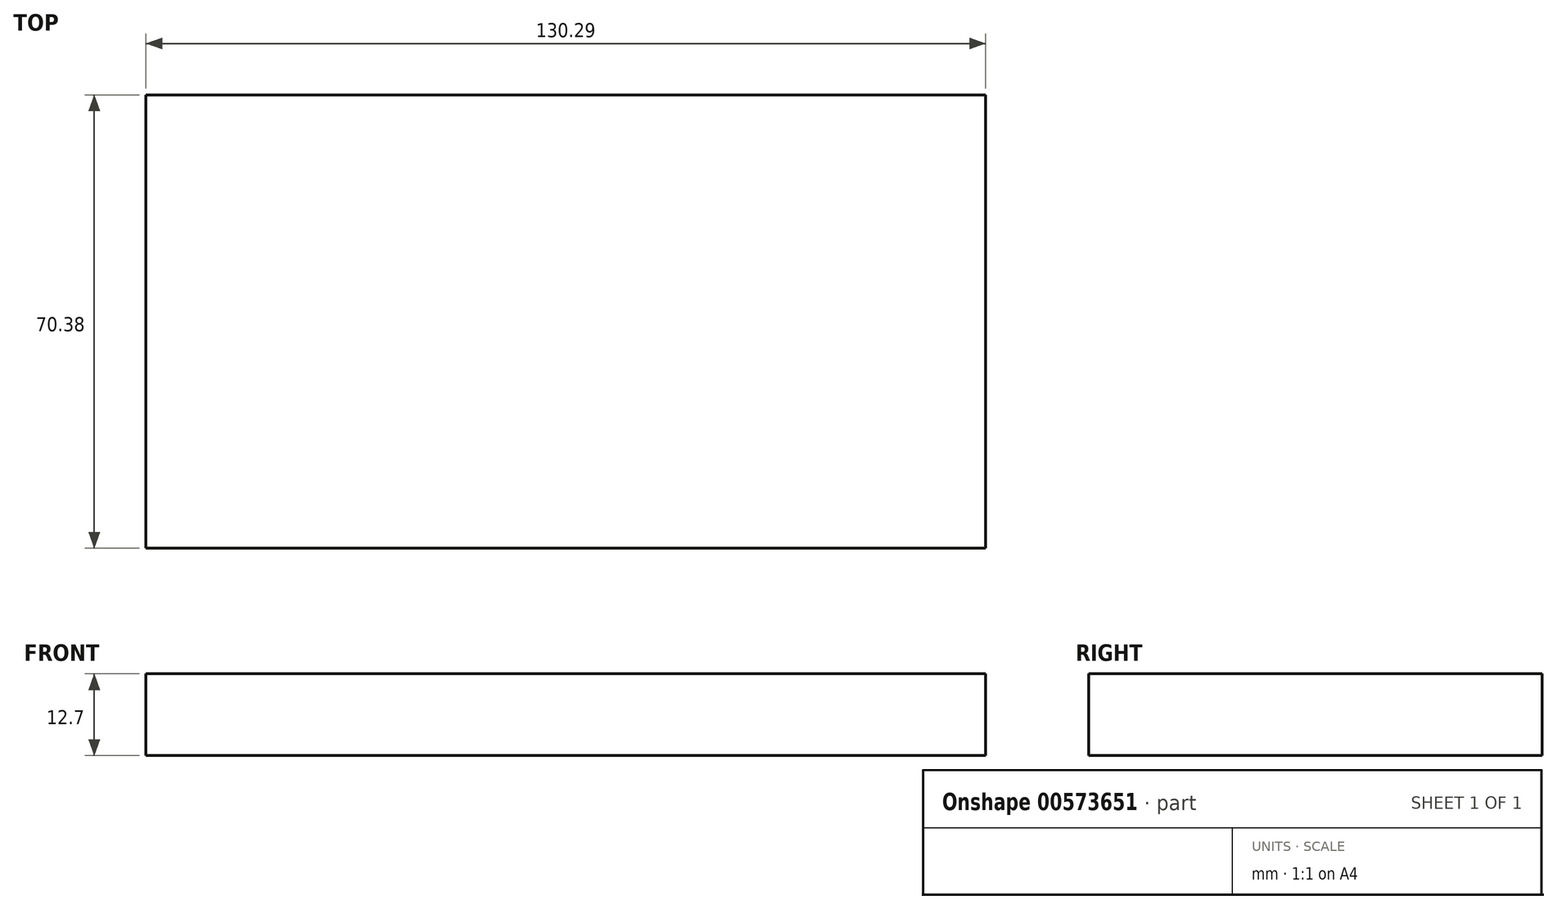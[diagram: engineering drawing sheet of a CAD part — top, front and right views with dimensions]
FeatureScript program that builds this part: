
annotation { "Feature Type Name" : "Feature", "Feature Type Description" : "" }
export const myFeature = defineFeature(function(context is Context, id is Id, definition is map)
    precondition{}
    {
        {
            var Q0;
            Q0=qCreatedBy(makeId("Top.planeOp"),FACE);
            var sketch = newSketch(context, id + "F0", { "sketchPlane" : qUnion([Q0])});
            skLineSegment(sketch, "E0.bottom", {"start": v(-55.15, -24.58) * mm, "end": v(75.14, -24.58) * mm});
            skLineSegment(sketch, "E0.top", {"start": v(-55.15, 45.8) * mm, "end": v(75.14, 45.8) * mm});
            skLineSegment(sketch, "E0.left", {"start": v(-55.15, -24.58) * mm, "end": v(-55.15, 45.8) * mm});
            skLineSegment(sketch, "E0.right", {"start": v(75.14, -24.58) * mm, "end": v(75.14, 45.8) * mm});
            skSolve(sketch);
        }
        {
            var Q0;
            Q0=makeQuery(id+"F0.imprint","IMPRINT",FACE,{"disambiguationData":[TD([[makeQuery(id+"F0.imprint","IMPRINT",EDGE,{"derivedFrom":sQuery(id+"F0.wireOp",EDGE,"E0.bottom")}),1.0]])]});
            extrude(context, id + "F1", {"entities" : qUnion([Q0]), "depth" : 12.7 * mm, "offsetDistance" : 25.4 * mm});
        }
    });
